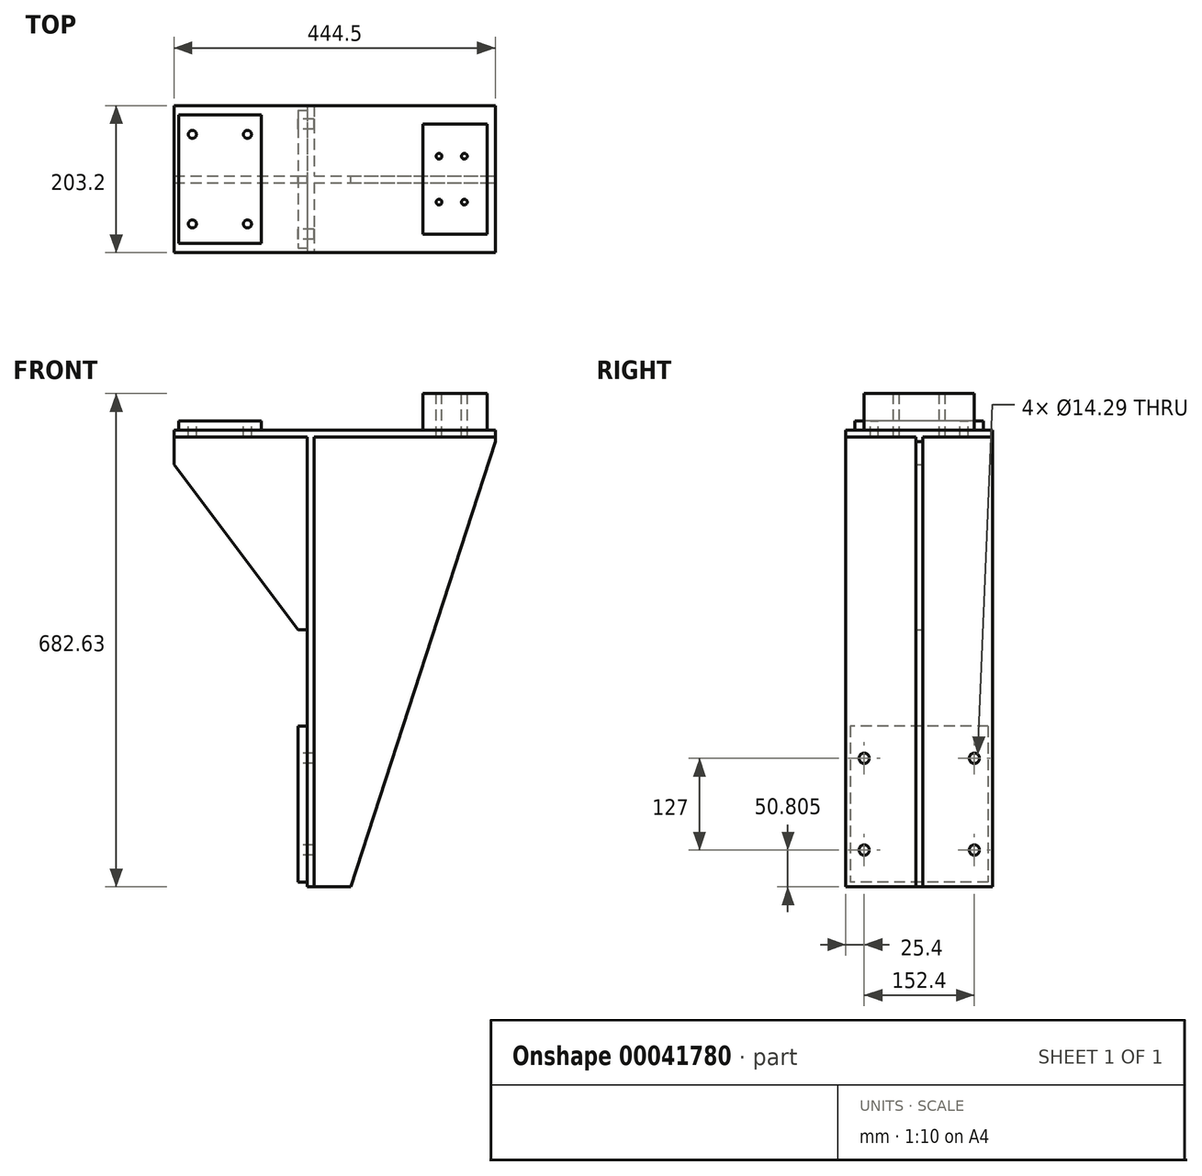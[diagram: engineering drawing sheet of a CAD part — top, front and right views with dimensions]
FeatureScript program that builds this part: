
annotation { "Feature Type Name" : "Feature", "Feature Type Description" : "" }
export const myFeature = defineFeature(function(context is Context, id is Id, definition is map)
    precondition{}
    {
        {
            var Q0;
            Q0=qCreatedBy(makeId("Top.planeOp"),FACE);
            var sketch = newSketch(context, id + "F0", { "sketchPlane" : qUnion([Q0])});
            skLineSegment(sketch, "E0.rect.bottom", {"start": v(-222.25, 101.6) * mm, "end": v(222.25, 101.6) * mm});
            skLineSegment(sketch, "E0.rect.top", {"start": v(-222.25, -101.6) * mm, "end": v(222.25, -101.6) * mm});
            skLineSegment(sketch, "E0.rect.left", {"start": v(-222.25, 101.6) * mm, "end": v(-222.25, -101.6) * mm});
            skLineSegment(sketch, "E0.rect.right", {"start": v(222.25, 101.6) * mm, "end": v(222.25, -101.6) * mm});
            skPoint(sketch, "E0.rect.middle", {"position": v(0, 0) * mm});
            skSolve(sketch);
        }
        {
            var Q0;
            Q0 = qSketchRegion(id + "F0", true);
            extrude(context, id + "F1", {"entities" : qUnion([Q0]), "oppositeDirection" : true, "depth" : 9.52 * mm});
        }
        {
            var Q0;
            Q0=makeQuery(id+"F1.opExtrude","CAP_FACE",FACE,{"disambiguationData":[OSD([sQuery(id+"F0.wireOp",EDGE,"E0.rect.bottom"),sQuery(id+"F0.wireOp",EDGE,"E0.rect.top"),sQuery(id+"F0.wireOp",EDGE,"E0.rect.left"),sQuery(id+"F0.wireOp",EDGE,"E0.rect.right")])],"isStart":true});
            var sketch = newSketch(context, id + "F2", { "sketchPlane" : qUnion([Q0])});
            skLineSegment(sketch, "E1.0", {"start": v(-158.75, 101.6) * mm, "end": v(-158.75, -101.6) * mm, "construction": true});
            skLineSegment(sketch, "E2.0", {"start": v(-215.9, 101.6) * mm, "end": v(-215.9, -101.6) * mm, "construction": true});
            skLineSegment(sketch, "E3.MirrorCS", {"start": v(-101.6, 101.6) * mm, "end": v(-101.6, -101.6) * mm, "construction": true});
            skLineSegment(sketch, "E4", {"start": v(-247.12, 0) * mm, "end": v(246.46, 0) * mm, "construction": true});
            skLineSegment(sketch, "E5.0", {"start": v(-247.12, 88.9) * mm, "end": v(246.46, 88.9) * mm, "construction": true});
            skLineSegment(sketch, "E6.MirrorCS", {"start": v(-247.12, -88.9) * mm, "end": v(246.46, -88.9) * mm, "construction": true});
            skLineSegment(sketch, "E7.bottom", {"start": v(-215.9, 88.9) * mm, "end": v(-101.6, 88.9) * mm});
            skLineSegment(sketch, "E7.top", {"start": v(-215.9, -88.9) * mm, "end": v(-101.6, -88.9) * mm});
            skLineSegment(sketch, "E7.left", {"start": v(-215.9, 88.9) * mm, "end": v(-215.9, -88.9) * mm});
            skLineSegment(sketch, "E7.right", {"start": v(-101.6, 88.9) * mm, "end": v(-101.6, -88.9) * mm});
            skSolve(sketch);
        }
        {
            var Q0;
            Q0 = qSketchRegion(id + "F2", true);
            extrude(context, id + "F3", {"entities" : qUnion([Q0]), "operationType" : NewBodyOperationType.ADD, "depth" : 12.7 * mm});
        }
        {
            var Q0;
            Q0=makeQuery(id+"F3.opExtrude","CAP_FACE",FACE,{"disambiguationData":[OSD([sQuery(id+"F2.wireOp",EDGE,"E7.bottom"),sQuery(id+"F2.wireOp",EDGE,"E7.top"),sQuery(id+"F2.wireOp",EDGE,"E7.left"),sQuery(id+"F2.wireOp",EDGE,"E7.right")])],"isStart":false});
            var sketch = newSketch(context, id + "F4", { "sketchPlane" : qUnion([Q0])});
            skLineSegment(sketch, "E8", {"start": v(-158.75, 88.9) * mm, "end": v(-158.75, -88.9) * mm, "construction": true});
            skLineSegment(sketch, "E9", {"start": v(-215.9, 0) * mm, "end": v(-101.6, 0) * mm, "construction": true});
            skLineSegment(sketch, "E10.0", {"start": v(-215.9, 61.98) * mm, "end": v(-101.6, 61.98) * mm, "construction": true});
            skLineSegment(sketch, "E11.0", {"start": v(-196.85, 88.9) * mm, "end": v(-196.85, -88.9) * mm, "construction": true});
            skPoint(sketch, "E12", {"position": v(-196.85, 61.98) * mm});
            skPoint(sketch, "E13.MirrorP", {"position": v(-120.65, 61.98) * mm});
            skPoint(sketch, "E14.MirrorP", {"position": v(-120.65, -61.98) * mm});
            skPoint(sketch, "E15.MirrorP", {"position": v(-196.85, -61.98) * mm});
            skSolve(sketch);
        }
        {
            var Q0;
            Q0=sQuery(id+"F4.wireOp",VERTEX,"E12");
            var Q1;
            Q1=sQuery(id+"F4.wireOp",VERTEX,"E13.MirrorP");
            var Q2;
            Q2=sQuery(id+"F4.wireOp",VERTEX,"E15.MirrorP");
            var Q3;
            Q3=sQuery(id+"F4.wireOp",VERTEX,"E14.MirrorP");
            var Q4;
            Q4=makeQuery(id+"F1.opExtrude","SWEPT_BODY",BODY,{"disambiguationData":[OSD([sQuery(id+"F0.wireOp",EDGE,"E0.rect.bottom"),sQuery(id+"F0.wireOp",EDGE,"E0.rect.top"),sQuery(id+"F0.wireOp",EDGE,"E0.rect.left"),sQuery(id+"F0.wireOp",EDGE,"E0.rect.right")])]});
            hole(context, id + "F5", {"style" : HoleStyle.SIMPLE, "holeDiameter" : 11.1 * mm, "endStyle" : HoleEndStyle.THROUGH, "locations" : qUnion([Q0, Q1, Q2, Q3]), "scope" : qUnion([Q4])});
        }
        {
            var Q0;
            Q0=makeQuery(id+"F1.opExtrude","CAP_FACE",FACE,{"disambiguationData":[OSD([sQuery(id+"F0.wireOp",EDGE,"E0.rect.bottom"),sQuery(id+"F0.wireOp",EDGE,"E0.rect.top"),sQuery(id+"F0.wireOp",EDGE,"E0.rect.left"),sQuery(id+"F0.wireOp",EDGE,"E0.rect.right")])],"isStart":true});
            var sketch = newSketch(context, id + "F6", { "sketchPlane" : qUnion([Q0])});
            skLineSegment(sketch, "E16.0", {"start": v(-215.9, -88.9) * mm, "end": v(-101.6, -88.9) * mm, "construction": true});
            skLineSegment(sketch, "E17", {"start": v(-158.75, -88.9) * mm, "end": v(-158.75, 123.27) * mm, "construction": true});
            skLineSegment(sketch, "E18.0", {"start": v(161.93, -88.9) * mm, "end": v(161.92, 123.27) * mm, "construction": true});
            skLineSegment(sketch, "E19.0", {"start": v(122.3, -88.9) * mm, "end": v(122.3, 123.27) * mm, "construction": true});
            skLineSegment(sketch, "E20.0", {"start": v(211.2, -88.9) * mm, "end": v(211.2, 123.27) * mm, "construction": true});
            skLineSegment(sketch, "E21.0", {"start": v(-222.25, 101.6) * mm, "end": v(-222.25, -101.6) * mm, "construction": true});
            skLineSegment(sketch, "E22", {"start": v(-222.25, 0) * mm, "end": v(238.55, 0) * mm, "construction": true});
            skLineSegment(sketch, "E23.0", {"start": v(-222.25, 76.2) * mm, "end": v(238.55, 76.2) * mm, "construction": true});
            skLineSegment(sketch, "E24.bottom", {"start": v(122.3, 76.2) * mm, "end": v(211.2, 76.2) * mm});
            skLineSegment(sketch, "E24.top", {"start": v(122.3, -76.2) * mm, "end": v(211.2, -76.2) * mm});
            skLineSegment(sketch, "E24.left", {"start": v(122.3, 76.2) * mm, "end": v(122.3, -76.2) * mm});
            skLineSegment(sketch, "E24.right", {"start": v(211.2, 76.2) * mm, "end": v(211.2, -76.2) * mm});
            skSolve(sketch);
        }
        {
            var Q0;
            Q0 = qSketchRegion(id + "F6", true);
            extrude(context, id + "F7", {"entities" : qUnion([Q0]), "operationType" : NewBodyOperationType.ADD, "depth" : 50.8 * mm});
        }
        {
            var Q0;
            Q0=makeQuery(id+"F7.opExtrude","CAP_FACE",FACE,{"disambiguationData":[OSD([sQuery(id+"F6.wireOp",EDGE,"E24.bottom"),sQuery(id+"F6.wireOp",EDGE,"E24.top"),sQuery(id+"F6.wireOp",EDGE,"E24.left"),sQuery(id+"F6.wireOp",EDGE,"E24.right")])],"isStart":false});
            var sketch = newSketch(context, id + "F8", { "sketchPlane" : qUnion([Q0])});
            skLineSegment(sketch, "E25.0", {"start": v(161.93, -88.9) * mm, "end": v(161.92, 123.27) * mm, "construction": true});
            skLineSegment(sketch, "E26.0", {"start": v(144.4, -88.9) * mm, "end": v(144.4, 123.27) * mm, "construction": true});
            skLineSegment(sketch, "E27.0", {"start": v(-222.25, 0) * mm, "end": v(238.55, 0) * mm, "construction": true});
            skLineSegment(sketch, "E28.0", {"start": v(-222.25, 31.75) * mm, "end": v(238.55, 31.75) * mm, "construction": true});
            skPoint(sketch, "E29", {"position": v(144.4, 31.75) * mm});
            skPoint(sketch, "E30.MirrorP", {"position": v(179.45, 31.75) * mm});
            skPoint(sketch, "E31.MirrorP", {"position": v(144.4, -31.75) * mm});
            skPoint(sketch, "E32.MirrorP", {"position": v(179.45, -31.75) * mm});
            skSolve(sketch);
        }
        {
            var Q0;
            Q0=sQuery(id+"F8.wireOp",VERTEX,"E29");
            var Q1;
            Q1=sQuery(id+"F8.wireOp",VERTEX,"E30.MirrorP");
            var Q2;
            Q2=sQuery(id+"F8.wireOp",VERTEX,"E31.MirrorP");
            var Q3;
            Q3=sQuery(id+"F8.wireOp",VERTEX,"E32.MirrorP");
            var Q4;
            Q4=makeQuery(id+"F1.opExtrude","SWEPT_BODY",BODY,{"disambiguationData":[OSD([sQuery(id+"F0.wireOp",EDGE,"E0.rect.bottom"),sQuery(id+"F0.wireOp",EDGE,"E0.rect.top"),sQuery(id+"F0.wireOp",EDGE,"E0.rect.left"),sQuery(id+"F0.wireOp",EDGE,"E0.rect.right")])]});
            hole(context, id + "F9", {"style" : HoleStyle.SIMPLE, "holeDiameter" : 7.94 * mm, "endStyle" : HoleEndStyle.THROUGH, "locations" : qUnion([Q0, Q1, Q2, Q3]), "scope" : qUnion([Q4])});
        }
        {
            var Q0;
            Q0=makeQuery(id+"F1.opExtrude","SWEPT_FACE",FACE,{"disambiguationData":[OSD([sQuery(id+"F0.wireOp",EDGE,"E0.rect.left")])]});
            cPlane(context, id + "F10", {"entities" : qUnion([Q0]), "cplaneType" : CPlaneType.OFFSET, "offset" : 184.15 * mm, "oppositeDirection" : true, "width" : 152.4 * mm, "height" : 152.4 * mm});
        }
        {
            var Q0;
            Q0=qCreatedBy(id+"F10.planeOp",FACE);
            var sketch = newSketch(context, id + "F11", { "sketchPlane" : qUnion([Q0])});
            skLineSegment(sketch, "E33.0", {"start": v(-101.6, -9.53) * mm, "end": v(101.6, -9.53) * mm});
            skLineSegment(sketch, "E34.0", {"start": v(-101.6, -631.83) * mm, "end": v(101.6, -631.83) * mm});
            skLineSegment(sketch, "E35", {"start": v(-101.6, -9.53) * mm, "end": v(-101.6, -631.83) * mm});
            skLineSegment(sketch, "E36", {"start": v(101.6, -9.53) * mm, "end": v(101.6, -631.83) * mm});
            skSolve(sketch);
        }
        {
            var Q0;
            Q0 = qSketchRegion(id + "F11", true);
            extrude(context, id + "F12", {"entities" : qUnion([Q0]), "operationType" : NewBodyOperationType.ADD, "oppositeDirection" : true, "depth" : 9.52 * mm});
        }
        {
            var Q0;
            Q0=qCreatedBy(makeId("Front.planeOp"),FACE);
            var sketch = newSketch(context, id + "F13", { "sketchPlane" : qUnion([Q0])});
            skLineSegment(sketch, "E37.0", {"start": v(-222.25, -9.53) * mm, "end": v(-38.1, -9.53) * mm});
            skLineSegment(sketch, "E38.0", {"start": v(-38.1, -9.53) * mm, "end": v(-38.1, -631.83) * mm});
            skLineSegment(sketch, "E39", {"start": v(-222.25, -9.52) * mm, "end": v(-222.25, -47.63) * mm});
            skLineSegment(sketch, "E40", {"start": v(-222.25, -47.62) * mm, "end": v(-50.8, -276.23) * mm});
            skLineSegment(sketch, "E41", {"start": v(-50.8, -276.23) * mm, "end": v(-38.1, -276.23) * mm});
            skSolve(sketch);
        }
        {
            var Q0;
            Q0 = qSketchRegion(id + "F13", true);
            extrude(context, id + "F14", {"entities" : qUnion([Q0]), "operationType" : NewBodyOperationType.ADD, "endBound" : BoundingType.SYMMETRIC, "depth" : 9.52 * mm});
        }
        {
            var Q0;
            Q0=qCreatedBy(makeId("Front.planeOp"),FACE);
            var sketch = newSketch(context, id + "F15", { "sketchPlane" : qUnion([Q0])});
            skLineSegment(sketch, "E42.0", {"start": v(-28.58, -9.53) * mm, "end": v(222.25, -9.53) * mm});
            skLineSegment(sketch, "E43.0", {"start": v(-28.58, -9.53) * mm, "end": v(-28.58, -631.83) * mm});
            skLineSegment(sketch, "E44", {"start": v(-28.58, -631.83) * mm, "end": v(22.22, -631.83) * mm});
            skLineSegment(sketch, "E45", {"start": v(22.22, -631.83) * mm, "end": v(222.25, -15.87) * mm});
            skLineSegment(sketch, "E46", {"start": v(222.25, -15.88) * mm, "end": v(222.25, -9.52) * mm});
            skSolve(sketch);
        }
        {
            var Q0;
            Q0 = qSketchRegion(id + "F15", true);
            extrude(context, id + "F16", {"entities" : qUnion([Q0]), "operationType" : NewBodyOperationType.ADD, "endBound" : BoundingType.SYMMETRIC, "depth" : 9.52 * mm});
        }
        {
            var Q0;
            Q0=makeQuery(id+"F12.opExtrude","CAP_FACE",FACE,{"disambiguationData":[OSD([sQuery(id+"F11.wireOp",EDGE,"E33.0"),sQuery(id+"F11.wireOp",EDGE,"E34.0"),sQuery(id+"F11.wireOp",EDGE,"E35"),sQuery(id+"F11.wireOp",EDGE,"E36")])],"isStart":true});
            var sketch = newSketch(context, id + "F17", { "sketchPlane" : qUnion([Q0])});
            skLineSegment(sketch, "E47.0", {"start": v(-101.6, -9.53) * mm, "end": v(-101.6, -631.83) * mm, "construction": true});
            skLineSegment(sketch, "E48.0", {"start": v(-101.6, -631.83) * mm, "end": v(101.6, -631.83) * mm, "construction": true});
            skLineSegment(sketch, "E49.0", {"start": v(101.6, -9.53) * mm, "end": v(101.6, -631.83) * mm, "construction": true});
            skLineSegment(sketch, "E50.0", {"start": v(-101.6, -625.48) * mm, "end": v(101.6, -625.48) * mm, "construction": true});
            skLineSegment(sketch, "E51.0", {"start": v(-101.6, -409.58) * mm, "end": v(101.6, -409.58) * mm, "construction": true});
            skLineSegment(sketch, "E52.0", {"start": v(-95.25, -9.53) * mm, "end": v(-95.25, -631.83) * mm, "construction": true});
            skLineSegment(sketch, "E53.bottom", {"start": v(-95.25, -409.58) * mm, "end": v(95.25, -409.58) * mm});
            skLineSegment(sketch, "E53.top", {"start": v(-95.25, -625.48) * mm, "end": v(95.25, -625.48) * mm});
            skLineSegment(sketch, "E53.left", {"start": v(-95.25, -409.58) * mm, "end": v(-95.25, -625.48) * mm});
            skLineSegment(sketch, "E53.right", {"start": v(95.25, -409.58) * mm, "end": v(95.25, -625.48) * mm});
            skSolve(sketch);
        }
        {
            var Q0;
            Q0 = qSketchRegion(id + "F17", true);
            extrude(context, id + "F18", {"entities" : qUnion([Q0]), "operationType" : NewBodyOperationType.ADD, "depth" : 12.7 * mm});
        }
        {
            var Q0;
            Q0=makeQuery(id+"F18.opExtrude","CAP_FACE",FACE,{"disambiguationData":[OSD([sQuery(id+"F17.wireOp",EDGE,"E53.bottom"),sQuery(id+"F17.wireOp",EDGE,"E53.top"),sQuery(id+"F17.wireOp",EDGE,"E53.left"),sQuery(id+"F17.wireOp",EDGE,"E53.right")])],"isStart":false});
            var sketch = newSketch(context, id + "F19", { "sketchPlane" : qUnion([Q0])});
            skLineSegment(sketch, "E54.0", {"start": v(-95.25, -409.58) * mm, "end": v(95.25, -409.58) * mm, "construction": true});
            skLineSegment(sketch, "E55", {"start": v(0, -454.03) * mm, "end": v(0, -581.03) * mm, "construction": true});
            skPoint(sketch, "E55.endSnap0", {"position": v(0, -625.48) * mm});
            skLineSegment(sketch, "E56.0", {"start": v(-95.25, -454.03) * mm, "end": v(95.25, -454.03) * mm, "construction": true});
            skLineSegment(sketch, "E57.0", {"start": v(-95.25, -581.03) * mm, "end": v(95.25, -581.03) * mm, "construction": true});
            skLineSegment(sketch, "E58.0", {"start": v(-76.2, -409.58) * mm, "end": v(-76.2, -650.06) * mm, "construction": true});
            skPoint(sketch, "E59.orphan", {"position": v(0, -409.58) * mm});
            skPoint(sketch, "E60.trimOffspring.end.orphan", {"position": v(0, -650.06) * mm});
            skLineSegment(sketch, "E61", {"start": v(0, -517.53) * mm, "end": v(-162.58, -517.53) * mm, "construction": true});
            skPoint(sketch, "E62", {"position": v(-76.2, -454.03) * mm});
            skPoint(sketch, "E63", {"position": v(-76.2, -581.03) * mm});
            skPoint(sketch, "E64.MirrorP", {"position": v(76.2, -454.03) * mm});
            skPoint(sketch, "E65.MirrorP", {"position": v(76.2, -581.03) * mm});
            skSolve(sketch);
        }
        {
            var Q0;
            Q0=sQuery(id+"F19.wireOp",VERTEX,"E62");
            var Q1;
            Q1=sQuery(id+"F19.wireOp",VERTEX,"E64.MirrorP");
            var Q2;
            Q2=sQuery(id+"F19.wireOp",VERTEX,"E63");
            var Q3;
            Q3=sQuery(id+"F19.wireOp",VERTEX,"E65.MirrorP");
            var Q4;
            Q4=makeQuery(id+"F1.opExtrude","SWEPT_BODY",BODY,{"disambiguationData":[OSD([sQuery(id+"F0.wireOp",EDGE,"E0.rect.bottom"),sQuery(id+"F0.wireOp",EDGE,"E0.rect.top"),sQuery(id+"F0.wireOp",EDGE,"E0.rect.left"),sQuery(id+"F0.wireOp",EDGE,"E0.rect.right")])]});
            hole(context, id + "F20", {"style" : HoleStyle.SIMPLE, "holeDiameter" : 14.29 * mm, "endStyle" : HoleEndStyle.THROUGH, "locations" : qUnion([Q0, Q1, Q2, Q3]), "scope" : qUnion([Q4])});
        }
    });
